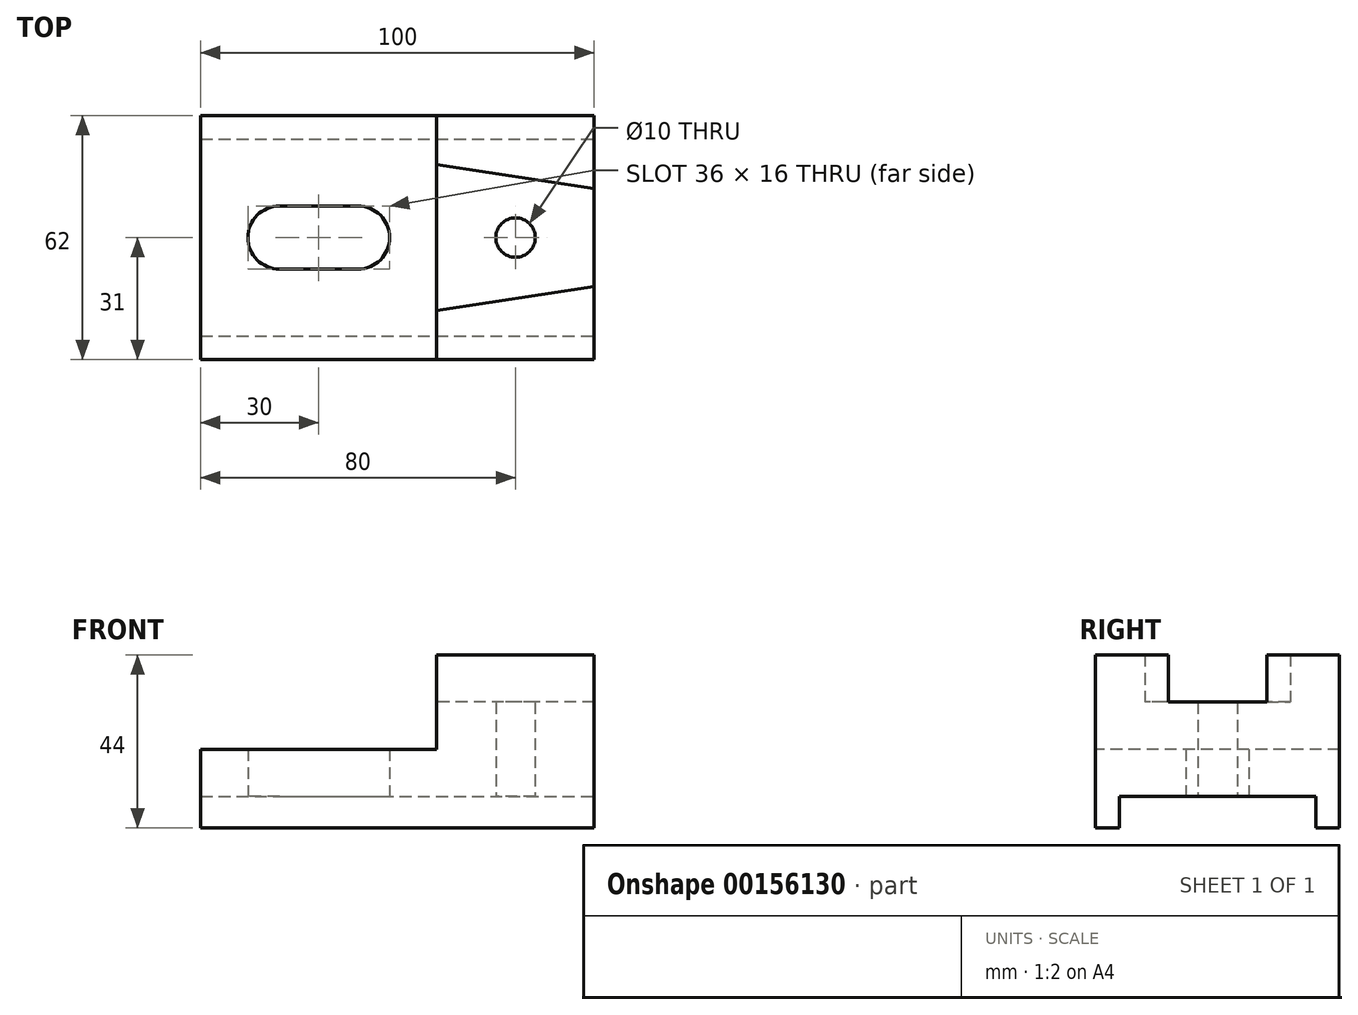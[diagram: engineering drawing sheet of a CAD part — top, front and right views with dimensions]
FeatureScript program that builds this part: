
annotation { "Feature Type Name" : "Feature", "Feature Type Description" : "" }
export const myFeature = defineFeature(function(context is Context, id is Id, definition is map)
    precondition{}
    {
        {
            var Q0;
            Q0=qCreatedBy(makeId("Top.planeOp"),FACE);
            var sketch = newSketch(context, id + "F0", { "sketchPlane" : qUnion([Q0])});
            skLineSegment(sketch, "E0.bottom", {"start": v(-30, 31) * mm, "end": v(30, 31) * mm});
            skLineSegment(sketch, "E0.top", {"start": v(-30, -31) * mm, "end": v(30, -31) * mm});
            skLineSegment(sketch, "E0.left", {"start": v(-30, 31) * mm, "end": v(-30, -31) * mm});
            skLineSegment(sketch, "E0.right", {"start": v(30, 31) * mm, "end": v(30, -31) * mm});
            skPoint(sketch, "E0.middle", {"position": v(0, 0) * mm});
            skLineSegment(sketch, "E1.bottom", {"start": v(30, 31) * mm, "end": v(70, 31) * mm});
            skLineSegment(sketch, "E1.top", {"start": v(30, -31) * mm, "end": v(70, -31) * mm});
            skLineSegment(sketch, "E1.right", {"start": v(70, 31) * mm, "end": v(70, -31) * mm});
            skPoint(sketch, "E1.middle", {"position": v(50, 0) * mm});
            skLineSegment(sketch, "E2", {"start": v(-30, 25) * mm, "end": v(70, 25) * mm});
            skLineSegment(sketch, "E3", {"start": v(-30, -25) * mm, "end": v(70, -25) * mm});
            skCircle(sketch, "E4", {"center": v(50, 0) * mm, "radius": 5 * mm});
            skLineSegment(sketch, "E5", {"start": v(30, 18.5) * mm, "end": v(70, 12.5) * mm});
            skLineSegment(sketch, "E6.MirrorCS", {"start": v(30, -18.5) * mm, "end": v(70, -12.5) * mm});
            skLineSegment(sketch, "E7.bottom", {"start": v(-10, 8) * mm, "end": v(10, 8) * mm});
            skLineSegment(sketch, "E7.top", {"start": v(-10, -8) * mm, "end": v(10, -8) * mm});
            skArc(sketch, "E8", {"start": v(-10, 8) * mm, "mid": v(-18, 0) * mm, "end": v(-10, -8) * mm});
            skArc(sketch, "E9", {"start": v(10, 8) * mm, "mid": v(18, 0) * mm, "end": v(10, -8) * mm});
            skPoint(sketch, "E10", {"position": v(-18, 0) * mm});
            skPoint(sketch, "E11", {"position": v(18, 0) * mm});
            skSolve(sketch);
        }
        {
            var Q0;
            {var subQ0=sQuery(id+"F0.wireOp",EDGE,"E0.top");Q0=makeQuery(id+"F0.imprint","IMPRINT",FACE,{"disambiguationData":[TD([[makeQuery(id+"F0.imprint","IMPRINT",EDGE,{"derivedFrom":subQ0}),1.0]])]});}
            var Q1;
            {var subQ0=sQuery(id+"F0.wireOp",EDGE,"E1.top");Q1=makeQuery(id+"F0.imprint","IMPRINT",FACE,{"disambiguationData":[TD([[makeQuery(id+"F0.imprint","IMPRINT",EDGE,{"derivedFrom":subQ0}),1.0]])]});}
            var Q2;
            {var subQ0=sQuery(id+"F0.wireOp",EDGE,"E0.bottom");Q2=makeQuery(id+"F0.imprint","IMPRINT",FACE,{"disambiguationData":[TD([[makeQuery(id+"F0.imprint","IMPRINT",EDGE,{"derivedFrom":subQ0}),-1.0]])]});}
            var Q3;
            {var subQ0=sQuery(id+"F0.wireOp",EDGE,"E1.bottom");Q3=makeQuery(id+"F0.imprint","IMPRINT",FACE,{"disambiguationData":[TD([[makeQuery(id+"F0.imprint","IMPRINT",EDGE,{"derivedFrom":subQ0}),-1.0]])]});}
            extrude(context, id + "F1", {"entities" : qUnion([Q0, Q1, Q2, Q3]), "oppositeDirection" : true, "depth" : 8 * mm});
        }
        {
            var Q0;
            {var subQ0=sQuery(id+"F0.wireOp",EDGE,"E0.bottom");Q0=makeQuery(id+"F0.imprint","IMPRINT",FACE,{"disambiguationData":[TD([[makeQuery(id+"F0.imprint","IMPRINT",EDGE,{"derivedFrom":subQ0}),-1.0]])]});}
            var Q1;
            Q1=makeQuery(id+"F0.imprint","IMPRINT",FACE,{"disambiguationData":[TD([[makeQuery(id+"F0.imprint","IMPRINT",EDGE,{"derivedFrom":sQuery(id+"F0.wireOp",EDGE,"E7.bottom")}),1.0]])]});
            var Q2;
            {var subQ0=sQuery(id+"F0.wireOp",EDGE,"E0.top");Q2=makeQuery(id+"F0.imprint","IMPRINT",FACE,{"disambiguationData":[TD([[makeQuery(id+"F0.imprint","IMPRINT",EDGE,{"derivedFrom":subQ0}),1.0]])]});}
            extrude(context, id + "F2", {"entities" : qUnion([Q0, Q1, Q2]), "operationType" : NewBodyOperationType.ADD, "depth" : 12 * mm});
        }
        {
            var Q0;
            {var subQ0=sQuery(id+"F0.wireOp",EDGE,"E1.bottom");Q0=makeQuery(id+"F0.imprint","IMPRINT",FACE,{"disambiguationData":[TD([[makeQuery(id+"F0.imprint","IMPRINT",EDGE,{"derivedFrom":subQ0}),-1.0]])]});}
            var Q1;
            {var subQ0=sQuery(id+"F0.wireOp",EDGE,"E5");Q1=makeQuery(id+"F0.imprint","IMPRINT",FACE,{"disambiguationData":[TD([[makeQuery(id+"F0.imprint","IMPRINT",EDGE,{"derivedFrom":subQ0}),1.0]])]});}
            var Q2;
            Q2=makeQuery(id+"F0.imprint","IMPRINT",FACE,{"disambiguationData":[TD([[makeQuery(id+"F0.imprint","IMPRINT",EDGE,{"derivedFrom":sQuery(id+"F0.wireOp",EDGE,"E4")}),-1.0]])]});
            var Q3;
            {var subQ0=sQuery(id+"F0.wireOp",EDGE,"E6.MirrorCS");Q3=makeQuery(id+"F0.imprint","IMPRINT",FACE,{"disambiguationData":[TD([[makeQuery(id+"F0.imprint","IMPRINT",EDGE,{"derivedFrom":subQ0}),-1.0]])]});}
            var Q4;
            {var subQ0=sQuery(id+"F0.wireOp",EDGE,"E1.top");Q4=makeQuery(id+"F0.imprint","IMPRINT",FACE,{"disambiguationData":[TD([[makeQuery(id+"F0.imprint","IMPRINT",EDGE,{"derivedFrom":subQ0}),1.0]])]});}
            extrude(context, id + "F3", {"entities" : qUnion([Q0, Q1, Q2, Q3, Q4]), "operationType" : NewBodyOperationType.ADD, "depth" : 24 * mm});
        }
        {
            var Q0;
            {var subQ0=sQuery(id+"F0.wireOp",EDGE,"E6.MirrorCS");Q0=makeQuery(id+"F0.imprint","IMPRINT",FACE,{"disambiguationData":[TD([[makeQuery(id+"F0.imprint","IMPRINT",EDGE,{"derivedFrom":subQ0}),-1.0]])]});}
            var Q1;
            {var subQ0=sQuery(id+"F0.wireOp",EDGE,"E1.top");Q1=makeQuery(id+"F0.imprint","IMPRINT",FACE,{"disambiguationData":[TD([[makeQuery(id+"F0.imprint","IMPRINT",EDGE,{"derivedFrom":subQ0}),1.0]])]});}
            var Q2;
            {var subQ0=sQuery(id+"F0.wireOp",EDGE,"E5");Q2=makeQuery(id+"F0.imprint","IMPRINT",FACE,{"disambiguationData":[TD([[makeQuery(id+"F0.imprint","IMPRINT",EDGE,{"derivedFrom":subQ0}),1.0]])]});}
            var Q3;
            {var subQ0=sQuery(id+"F0.wireOp",EDGE,"E1.bottom");Q3=makeQuery(id+"F0.imprint","IMPRINT",FACE,{"disambiguationData":[TD([[makeQuery(id+"F0.imprint","IMPRINT",EDGE,{"derivedFrom":subQ0}),-1.0]])]});}
            extrude(context, id + "F4", {"entities" : qUnion([Q0, Q1, Q2, Q3]), "operationType" : NewBodyOperationType.ADD, "depth" : 36 * mm});
        }
    });
